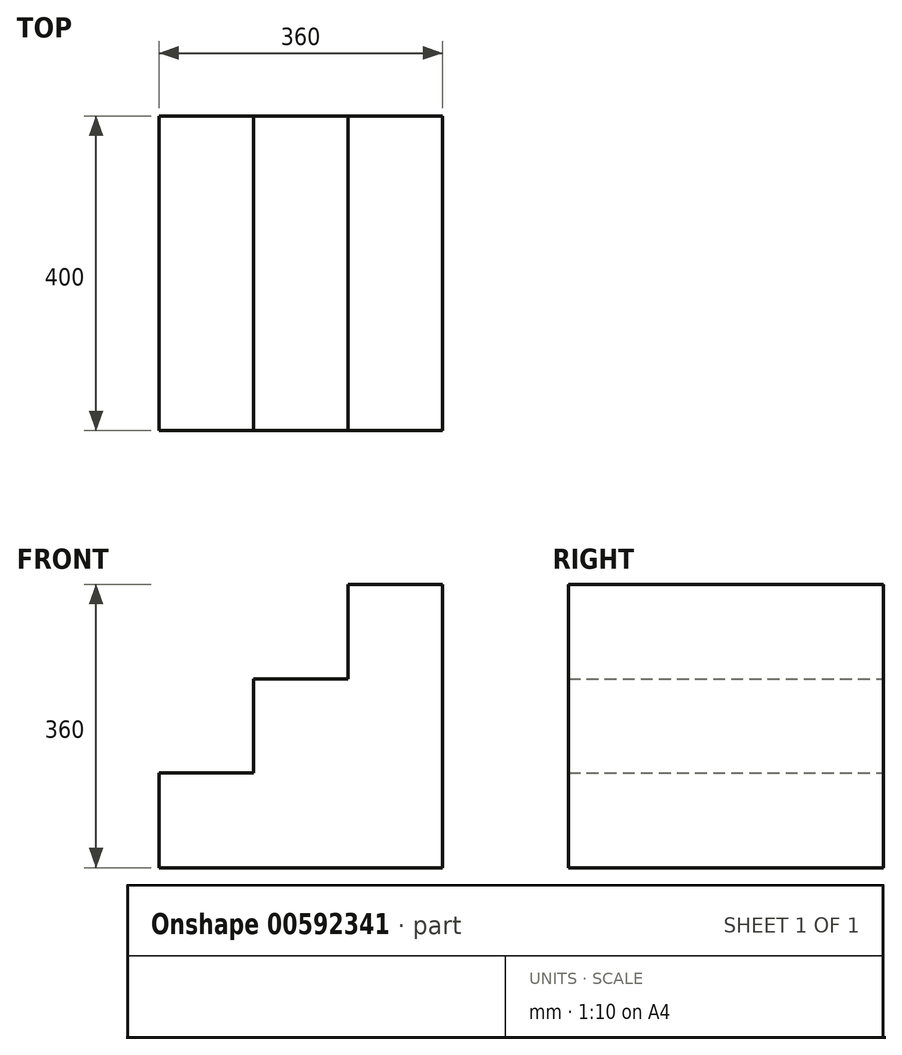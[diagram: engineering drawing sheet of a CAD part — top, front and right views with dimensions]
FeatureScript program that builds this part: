
annotation { "Feature Type Name" : "Feature", "Feature Type Description" : "" }
export const myFeature = defineFeature(function(context is Context, id is Id, definition is map)
    precondition{}
    {
        {
            var Q0;
            Q0=qCreatedBy(makeId("Front.planeOp"),FACE);
            var sketch = newSketch(context, id + "F0", { "sketchPlane" : qUnion([Q0])});
            skLineSegment(sketch, "E0", {"start": v(0, 0) * mm, "end": v(360, 0) * mm});
            skLineSegment(sketch, "E1", {"start": v(360, 0) * mm, "end": v(360, 360) * mm});
            skLineSegment(sketch, "E2", {"start": v(360, 360) * mm, "end": v(240, 360) * mm});
            skLineSegment(sketch, "E3", {"start": v(240, 360) * mm, "end": v(240, 240) * mm});
            skLineSegment(sketch, "E4", {"start": v(240, 240) * mm, "end": v(120, 240) * mm});
            skLineSegment(sketch, "E5", {"start": v(120, 240) * mm, "end": v(120, 120.31) * mm});
            skLineSegment(sketch, "E6", {"start": v(120, 120.31) * mm, "end": v(0, 120.31) * mm});
            skLineSegment(sketch, "E7", {"start": v(0, 0) * mm, "end": v(0, 120.31) * mm});
            skSolve(sketch);
        }
        {
            var Q0;
            Q0 = qSketchRegion(id + "F0", true);
            extrude(context, id + "F1", {"entities" : qUnion([Q0]), "depth" : 400 * mm, "offsetDistance" : 25 * mm});
        }
    });
